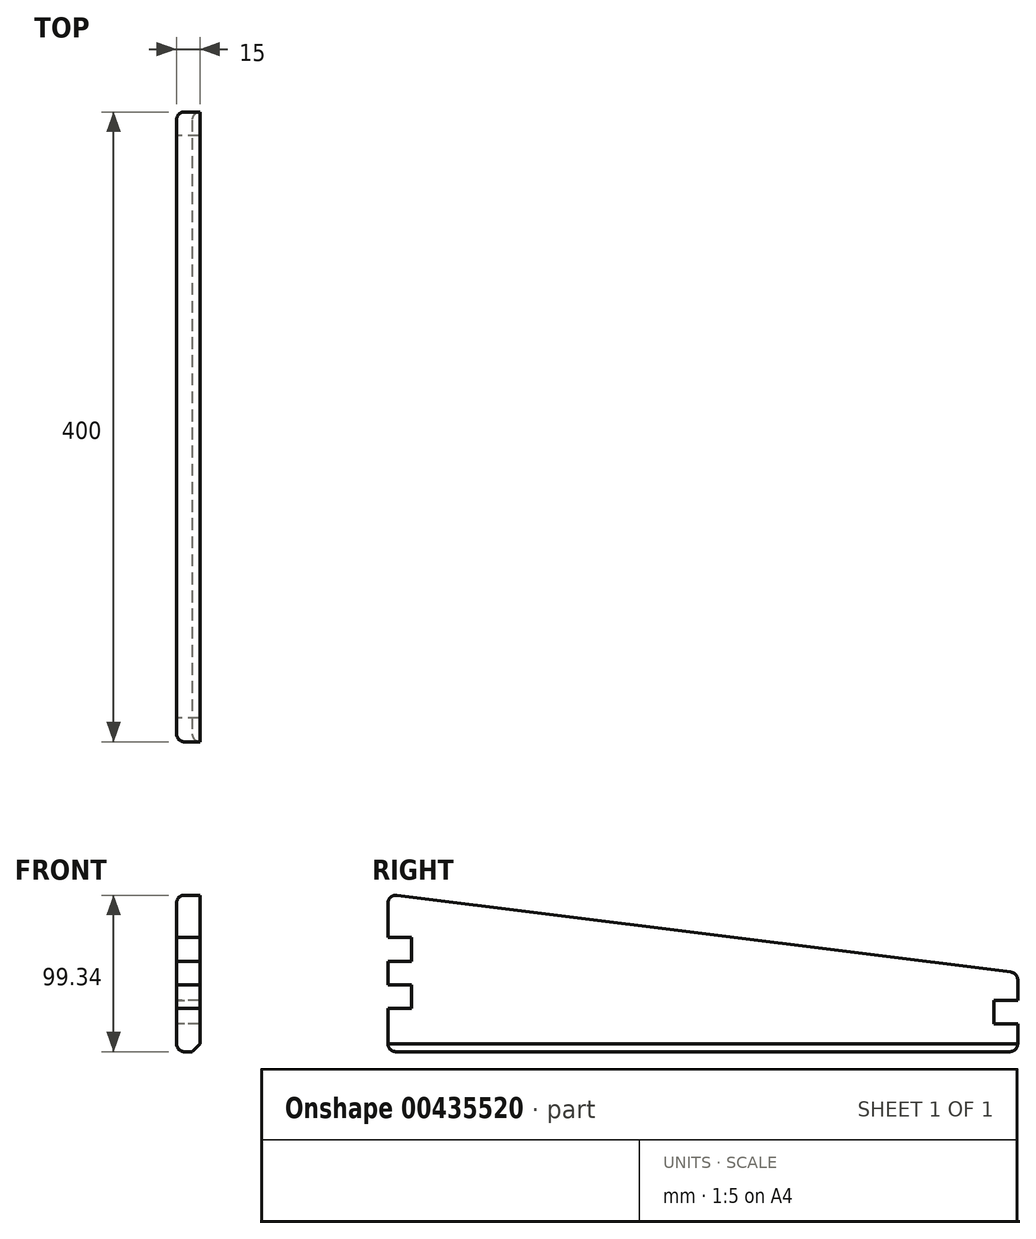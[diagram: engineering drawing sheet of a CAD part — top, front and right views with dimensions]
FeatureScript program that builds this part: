
annotation { "Feature Type Name" : "Feature", "Feature Type Description" : "" }
export const myFeature = defineFeature(function(context is Context, id is Id, definition is map)
    precondition{}
    {
        {
            var Q0;
            Q0=qCreatedBy(makeId("Right.planeOp"),FACE);
            var sketch = newSketch(context, id + "F0", { "sketchPlane" : qUnion([Q0])});
            skLineSegment(sketch, "E0.bottom", {"start": v(206.1, -35.37) * mm, "end": v(-193.9, -35.37) * mm});
            skPoint(sketch, "E0.middle", {"position": v(0, 0) * mm});
            skLineSegment(sketch, "E1", {"start": v(-193.9, 64.63) * mm, "end": v(206.1, 14.63) * mm});
            skLineSegment(sketch, "E2", {"start": v(-193.9, -7.87) * mm, "end": v(-178.9, -7.87) * mm});
            skLineSegment(sketch, "E3", {"start": v(-178.9, -7.87) * mm, "end": v(-178.9, 7.13) * mm});
            skLineSegment(sketch, "E4", {"start": v(-178.9, 7.13) * mm, "end": v(-193.9, 7.13) * mm});
            skLineSegment(sketch, "E5", {"start": v(-193.9, -7.87) * mm, "end": v(-193.9, -35.37) * mm});
            skLineSegment(sketch, "E6", {"start": v(-193.9, 7.13) * mm, "end": v(-193.9, 22.13) * mm});
            skLineSegment(sketch, "E7", {"start": v(-193.9, 22.13) * mm, "end": v(-178.9, 22.13) * mm});
            skLineSegment(sketch, "E8", {"start": v(-178.9, 22.13) * mm, "end": v(-178.9, 37.13) * mm});
            skLineSegment(sketch, "E9", {"start": v(-178.9, 37.13) * mm, "end": v(-193.9, 37.13) * mm});
            skLineSegment(sketch, "E10", {"start": v(-193.9, 64.63) * mm, "end": v(-193.9, 37.13) * mm});
            skLineSegment(sketch, "E11", {"start": v(206.1, -2.87) * mm, "end": v(191.1, -2.87) * mm});
            skLineSegment(sketch, "E12", {"start": v(191.1, -2.87) * mm, "end": v(191.1, -17.87) * mm});
            skLineSegment(sketch, "E13", {"start": v(191.1, -17.87) * mm, "end": v(206.1, -17.87) * mm});
            skLineSegment(sketch, "E14", {"start": v(206.1, 14.63) * mm, "end": v(206.1, -2.87) * mm});
            skLineSegment(sketch, "E15", {"start": v(206.1, -17.87) * mm, "end": v(206.1, -35.37) * mm});
            skSolve(sketch);
        }
        {
            var Q0;
            Q0=makeQuery(id+"F0.imprint","IMPRINT",FACE,{"disambiguationData":[TD([[makeQuery(id+"F0.imprint","IMPRINT",EDGE,{"derivedFrom":sQuery(id+"F0.wireOp",EDGE,"E0.bottom")}),-1.0]])]});
            extrude(context, id + "F1", {"entities" : qUnion([Q0]), "depth" : 15 * mm});
        }
        {
            var Q0;
            Q0=makeQuery(id+"F1.opExtrude","CAP_EDGE",EDGE,{"disambiguationData":[OSD([sQuery(id+"F0.wireOp",EDGE,"E14")])],"isStart":true});
            var Q1;
            Q1=makeQuery(id+"F1.opExtrude","CAP_EDGE",EDGE,{"disambiguationData":[OSD([sQuery(id+"F0.wireOp",EDGE,"E15")])],"isStart":true});
            var Q2;
            Q2=makeQuery(id+"F1.opExtrude","CAP_EDGE",EDGE,{"disambiguationData":[OSD([sQuery(id+"F0.wireOp",EDGE,"E10")])],"isStart":true});
            var Q3;
            Q3=makeQuery(id+"F1.opExtrude","CAP_EDGE",EDGE,{"disambiguationData":[OSD([sQuery(id+"F0.wireOp",EDGE,"E6")])],"isStart":true});
            var Q4;
            Q4=makeQuery(id+"F1.opExtrude","CAP_EDGE",EDGE,{"disambiguationData":[OSD([sQuery(id+"F0.wireOp",EDGE,"E5")])],"isStart":true});
            fillet(context, id + "F2", {"entities" : qUnion([Q0, Q1, Q2, Q3, Q4]), "radius" : 5 * mm, "tangentPropagation" : true, "allowEdgeOverflow" : false});
        }
        {
            var Q0;
            Q0=makeQuery(id+"F1.opExtrude","CAP_EDGE",EDGE,{"disambiguationData":[OSD([sQuery(id+"F0.wireOp",EDGE,"E0.bottom")])],"isStart":true});
            var Q1;
            Q1=makeQuery(id+"F1.opExtrude","CAP_EDGE",EDGE,{"disambiguationData":[OSD([sQuery(id+"F0.wireOp",EDGE,"E1")])],"isStart":true});
            fillet(context, id + "F3", {"entities" : qUnion([Q0, Q1]), "radius" : 5 * mm, "tangentPropagation" : true, "allowEdgeOverflow" : false});
        }
        {
            var Q0;
            Q0=makeQuery(id+"F1.opExtrude","CAP_EDGE",EDGE,{"disambiguationData":[OSD([sQuery(id+"F0.wireOp",EDGE,"E0.bottom")])],"isStart":false});
            chamfer(context, id + "F4", {"entities" : qUnion([Q0]), "width" : 5 * mm});
        }
    });
